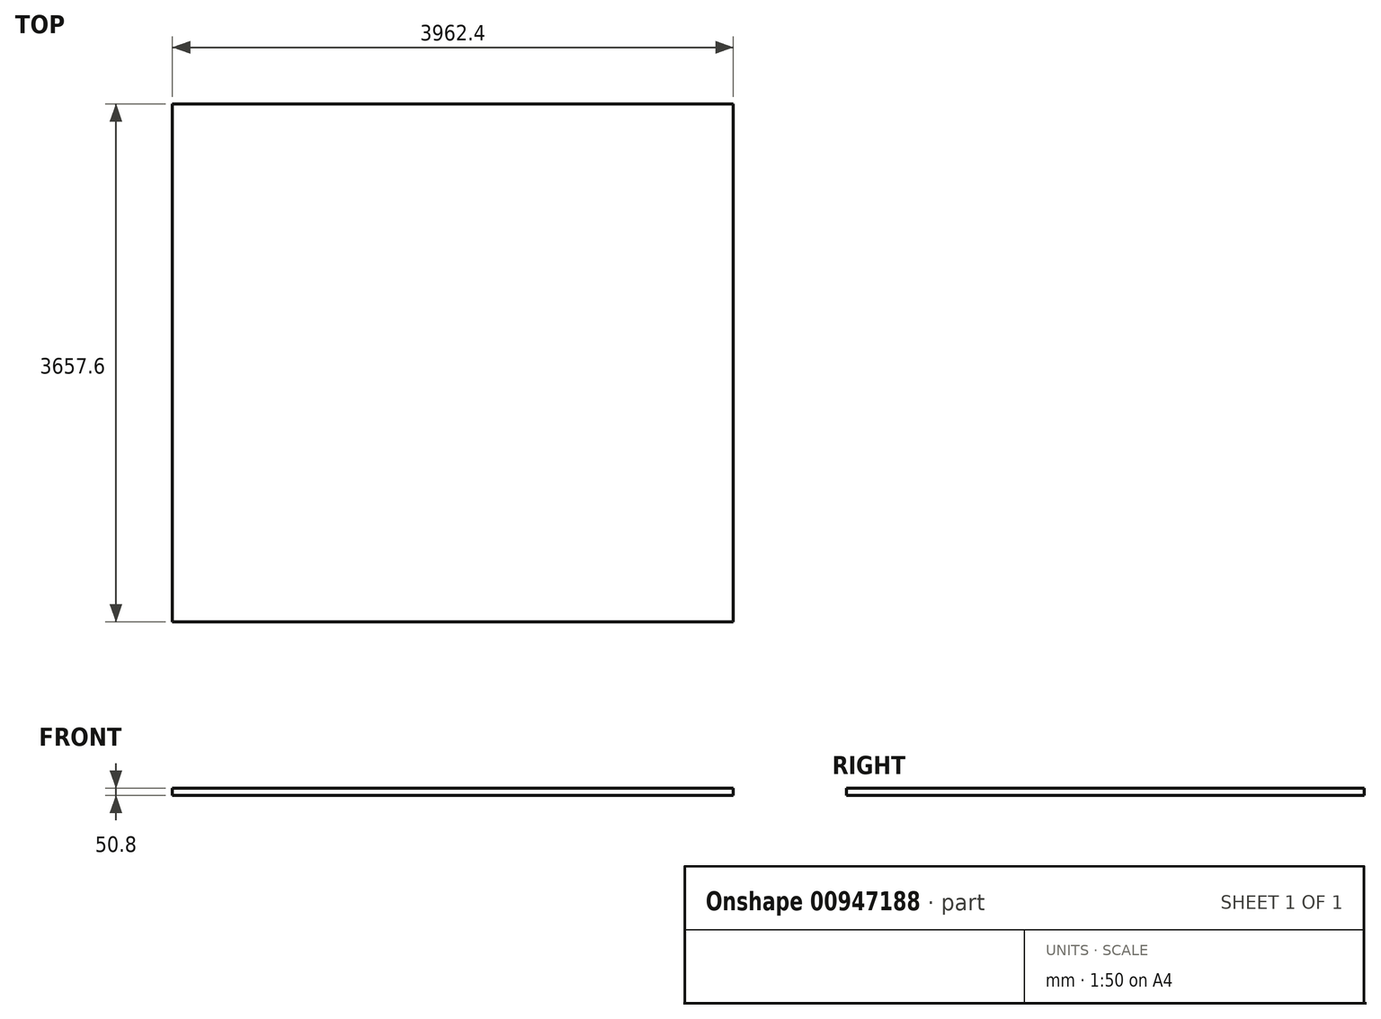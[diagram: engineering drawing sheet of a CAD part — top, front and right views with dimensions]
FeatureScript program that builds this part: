
annotation { "Feature Type Name" : "Feature", "Feature Type Description" : "" }
export const myFeature = defineFeature(function(context is Context, id is Id, definition is map)
    precondition{}
    {
        {
            var Q0;
            Q0=qCreatedBy(makeId("Top.planeOp"),FACE);
            var sketch = newSketch(context, id + "F0", { "sketchPlane" : qUnion([Q0])});
            skLineSegment(sketch, "E0.bottom", {"start": v(0, 0) * mm, "end": v(-3962.4, 0) * mm});
            skLineSegment(sketch, "E0.top", {"start": v(0, 3657.6) * mm, "end": v(-3962.4, 3657.6) * mm});
            skLineSegment(sketch, "E0.left", {"start": v(0, 0) * mm, "end": v(0, 3657.6) * mm});
            skLineSegment(sketch, "E0.right", {"start": v(-3962.4, 0) * mm, "end": v(-3962.4, 3657.6) * mm});
            skSolve(sketch);
        }
        {
            var Q0;
            Q0 = qSketchRegion(id + "F0", true);
            extrude(context, id + "F1", {"entities" : qUnion([Q0]), "depth" : 50.8 * mm, "offsetDistance" : 25.4 * mm});
        }
    });
